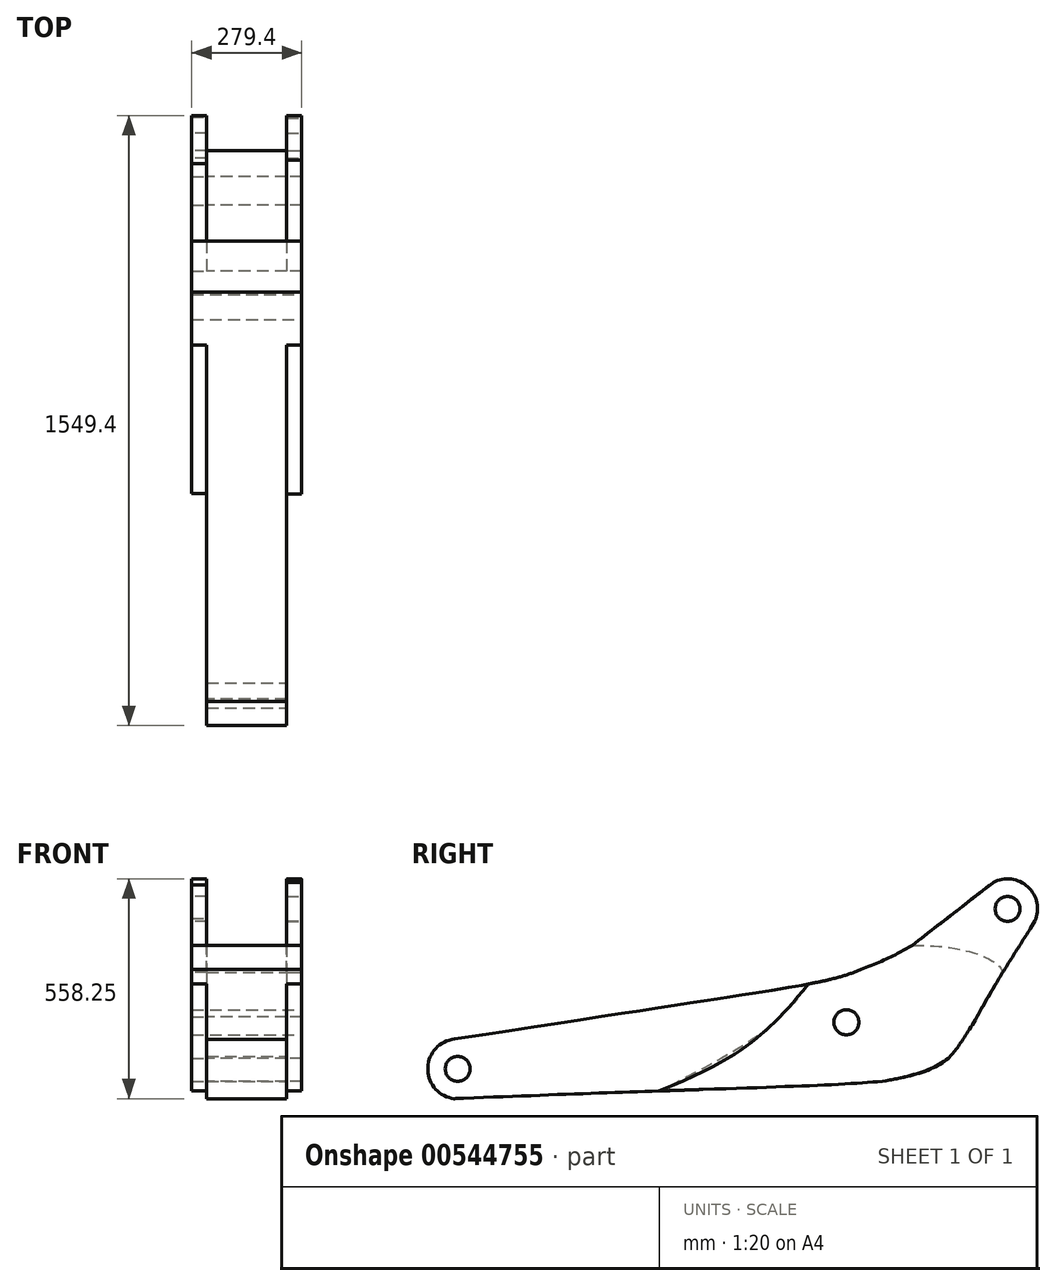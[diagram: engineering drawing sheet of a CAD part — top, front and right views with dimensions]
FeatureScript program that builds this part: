
annotation { "Feature Type Name" : "Feature", "Feature Type Description" : "" }
export const myFeature = defineFeature(function(context is Context, id is Id, definition is map)
    precondition{}
    {
        {
            var Q0;
            Q0=qCreatedBy(makeId("Right.planeOp"),FACE);
            var sketch = newSketch(context, id + "F0", { "sketchPlane" : qUnion([Q0])});
            skCircle(sketch, "E0", {"center": v(-987.29, 252.54) * mm, "radius": 76.2 * mm});
            skCircle(sketch, "E1", {"center": v(409.71, 658.94) * mm, "radius": 76.2 * mm});
            skFitSpline(sketch, "E2", {"points": [v(-996.45, 176.89) * mm, v(259.05, 279.13) * mm, v(396.8, 497.25) * mm], "startDerivative": vector(4754, 195.4) * mm, "endDerivative": vector(700.1, 1215.96) * mm});
            skFitSpline(sketch, "E3", {"points": [v(-1002.41, 327.22) * mm, v(37.1, 504.9) * mm, v(167.2, 566.13) * mm], "startDerivative": vector(3705.38, 571.7) * mm, "endDerivative": vector(553.4, 297.99) * mm});
            skFitSpline(sketch, "E4", {"points": [v(167.2, 566.13) * mm, v(396.8, 497.25) * mm], "startDerivative": vector(309.96, 11.48) * mm, "endDerivative": vector(22.96, -126.28) * mm});
            skFitSpline(sketch, "E5", {"points": [v(-364.35, 200.23) * mm, v(-36.22, 481.03) * mm], "startDerivative": vector(328.11, 280.9) * mm, "endDerivative": vector(328.11, 280.9) * mm});
            skFitSpline(sketch, "E6", {"points": [v(167.2, 566.13) * mm, v(374.05, 726.27) * mm], "startDerivative": vector(206.28, 161.2) * mm, "endDerivative": vector(206.28, 161.2) * mm});
            skFitSpline(sketch, "E7", {"points": [v(396.8, 497.25) * mm, v(480.72, 631.3) * mm], "startDerivative": vector(83.86, 134.07) * mm, "endDerivative": vector(83.86, 134.07) * mm});
            skFitSpline(sketch, "E8", {"points": [v(-36.22, 481.03) * mm, v(37.1, 504.9) * mm, v(117.46, 539.34) * mm, v(167.2, 566.13) * mm], "startDerivative": vector(208.85, 63.05) * mm, "endDerivative": vector(157.2, 89.13) * mm});
            skFitSpline(sketch, "E9", {"points": [v(396.8, 497.25) * mm, v(324.1, 370.97) * mm, v(259.05, 279.13) * mm, v(94.5, 221.73) * mm, v(-364.35, 200.23) * mm], "startDerivative": vector(-361.02, -614.75) * mm, "endDerivative": vector(-1360.38, -16) * mm});
            skPoint(sketch, "E10", {"position": v(0, 370.97) * mm});
            skSolve(sketch);
        }
        {
            var Q0;
            {var subQ5=sQuery(id+"F0.wireOp",EDGE,"E5");Q0=makeQuery(id+"F0.imprint","IMPRINT",FACE,{"disambiguationData":[TD([[makeQuery(id+"F0.imprint","IMPRINT",EDGE,{"derivedFrom":subQ5}),1.0]])]});}
            var Q1;
            {var subQ0=sQuery(id+"F0.wireOp",EDGE,"E4");Q1=makeQuery(id+"F0.imprint","IMPRINT",FACE,{"disambiguationData":[TD([[makeQuery(id+"F0.imprint","IMPRINT",EDGE,{"derivedFrom":subQ0}),-1.0]])]});}
            var Q2;
            {var subQ0=sQuery(id+"F0.wireOp",EDGE,"E2");var subQ1=sQuery(id+"F0.wireOp",EDGE,"E0");var subQ2=makeQuery(id+"F0.imprint","INTERSECT",VERTEX,{"disambiguationData":[OD(0.0)],"derivedFrom":[subQ1,subQ0]});Q2=makeQuery(id+"F0.imprint","IMPRINT",FACE,{"disambiguationData":[TD([[makeQuery(id+"F0.imprint","IMPRINT",EDGE,{"disambiguationData":[TD([[subQ2,1.0]])],"derivedFrom":subQ1}),1.0]])]});}
            extrude(context, id + "F1", {"entities" : qUnion([Q0, Q1, Q2]), "depth" : 203.2 * mm, "offsetDistance" : 25.4 * mm});
        }
        {
            var Q0;
            Q0=makeQuery(id+"F1.opExtrude","CAP_FACE",FACE,{"disambiguationData":[OSD([sQuery(id+"F0.wireOp",EDGE,"E0"),sQuery(id+"F0.wireOp",EDGE,"E1"),sQuery(id+"F0.wireOp",EDGE,"E2"),sQuery(id+"F0.wireOp",EDGE,"E3"),sQuery(id+"F0.wireOp",EDGE,"E6"),sQuery(id+"F0.wireOp",EDGE,"E7"),sQuery(id+"F0.wireOp",EDGE,"E8"),sQuery(id+"F0.wireOp",EDGE,"E9")])],"isStart":false});
            var sketch = newSketch(context, id + "F2", { "sketchPlane" : qUnion([Q0])});
            skPoint(sketch, "E11", {"position": v(-987.29, 252.54) * mm});
            skPoint(sketch, "E12", {"position": v(409.71, 658.94) * mm});
            skPoint(sketch, "E13", {"position": v(0, 370.97) * mm});
            skSolve(sketch);
        }
        {
            var Q0;
            Q0=sQuery(id+"F2.wireOp",VERTEX,"E11");
            var Q1;
            Q1=sQuery(id+"F2.wireOp",VERTEX,"E13");
            var Q2;
            Q2=sQuery(id+"F2.wireOp",VERTEX,"E12");
            var Q3;
            Q3=makeQuery(id+"F1.opExtrude","SWEPT_BODY",BODY,{"disambiguationData":[OSD([sQuery(id+"F0.wireOp",EDGE,"E0"),sQuery(id+"F0.wireOp",EDGE,"E1"),sQuery(id+"F0.wireOp",EDGE,"E2"),sQuery(id+"F0.wireOp",EDGE,"E3"),sQuery(id+"F0.wireOp",EDGE,"E6"),sQuery(id+"F0.wireOp",EDGE,"E7"),sQuery(id+"F0.wireOp",EDGE,"E8"),sQuery(id+"F0.wireOp",EDGE,"E9")])]});
            hole(context, id + "F3", {"style" : HoleStyle.SIMPLE, "endStyle" : HoleEndStyle.THROUGH, "holeDiameter" : 63.5 * mm, "isTappedThrough" : true, "tappedDepth" : 12.7 * mm, "tapClearance" : 3, "locations" : qUnion([Q0, Q1, Q2]), "scope" : qUnion([Q3])});
        }
        {
            var Q0;
            Q0=makeQuery(id+"F1.opExtrude","CAP_FACE",FACE,{"disambiguationData":[OSD([sQuery(id+"F0.wireOp",EDGE,"E0"),sQuery(id+"F0.wireOp",EDGE,"E2"),sQuery(id+"F0.wireOp",EDGE,"E3"),sQuery(id+"F0.wireOp",EDGE,"E4"),sQuery(id+"F0.wireOp",EDGE,"E8"),sQuery(id+"F0.wireOp",EDGE,"E9")])],"isStart":false});
            var sketch = newSketch(context, id + "F4", { "sketchPlane" : qUnion([Q0])});
            skCircle(sketch, "E14", {"center": v(409.71, 658.94) * mm, "radius": 76.2 * mm});
            skPoint(sketch, "E15", {"position": v(-987.29, 252.54) * mm});
            skFitSpline(sketch, "E16", {"points": [v(167.2, 566.13) * mm, v(373.2, 725.82) * mm], "startDerivative": vector(205.34, 160.91) * mm, "endDerivative": vector(205.34, 160.91) * mm});
            skFitSpline(sketch, "E17", {"points": [v(396.8, 497.25) * mm, v(479.44, 628.2) * mm], "startDerivative": vector(82.58, 130.98) * mm, "endDerivative": vector(82.58, 130.98) * mm});
            skFitSpline(sketch, "E18", {"points": [v(-96.78, 468.18) * mm, v(-216.48, 340.33) * mm, v(-475.94, 196.43) * mm], "startDerivative": vector(-328.27, -414.7) * mm, "endDerivative": vector(-773.2, -310.98) * mm});
            skFitSpline(sketch, "E19", {"points": [v(-96.78, 468.18) * mm, v(37.1, 504.9) * mm, v(167.2, 566.13) * mm], "startDerivative": vector(273.15, 62.38) * mm, "endDerivative": vector(254.87, 133.31) * mm});
            skFitSpline(sketch, "E20", {"points": [v(396.8, 497.25) * mm, v(331.4, 384.1) * mm, v(259.05, 279.13) * mm, v(91.08, 221.23) * mm, v(-475.94, 196.43) * mm], "startDerivative": vector(-347.8, -585.35) * mm, "endDerivative": vector(-2799.03, -99.02) * mm});
            skSolve(sketch);
        }
        {
            var Q0;
            {var subQ21=sQuery(id+"F4.wireOp",EDGE,"E18");Q0=makeQuery(id+"F4.imprint","IMPRINT",FACE,{"disambiguationData":[TD([[makeQuery(id+"F4.imprint","IMPRINT",EDGE,{"derivedFrom":subQ21}),1.0]])]});}
            var Q1;
            {var subQ6=sQuery(id+"F0.wireOp",EDGE,"E4");var subQ8=makeQuery(id+"F1.opExtrude","CAP_EDGE",EDGE,{"disambiguationData":[OSD([subQ6])],"isStart":false});Q1=makeQuery(id+"F4.imprint","IMPRINT",FACE,{"disambiguationData":[TD([[makeQuery(id+"F4.imprint","IMPRINT",EDGE,{"derivedFrom":subQ8}),1.0]])]});}
            var Q2;
            {var subQ0=sQuery(id+"F4.wireOp",EDGE,"E16");var subQ1=sQuery(id+"F4.wireOp",EDGE,"E14");var subQ2=makeQuery(id+"F4.imprint","INTERSECT",VERTEX,{"disambiguationData":[OD(1.0)],"derivedFrom":[subQ1,subQ0]});Q2=makeQuery(id+"F4.imprint","IMPRINT",FACE,{"disambiguationData":[TD([[makeQuery(id+"F4.imprint","IMPRINT",EDGE,{"disambiguationData":[TD([[subQ2,-1.0]])],"derivedFrom":subQ1}),1.0]])]});}
            extrude(context, id + "F5", {"entities" : qUnion([Q0, Q1, Q2]), "operationType" : NewBodyOperationType.ADD, "depth" : 25.4 * mm, "offsetDistance" : 25.4 * mm});
        }
        {
            var Q0;
            Q0=makeQuery(id+"F5.opExtrude","CAP_FACE",FACE,{"disambiguationData":[OSD([sQuery(id+"F0.wireOp",EDGE,"E2"),sQuery(id+"F0.wireOp",EDGE,"E3"),sQuery(id+"F0.wireOp",EDGE,"E8"),sQuery(id+"F3.hole-1.sketch.wireOp",EDGE,"core_line_2"),sQuery(id+"F3.hole-1.sketch.wireOp",EDGE,"core_line_3"),sQuery(id+"F4.wireOp",EDGE,"E14"),sQuery(id+"F4.wireOp",EDGE,"E16"),sQuery(id+"F4.wireOp",EDGE,"E17"),sQuery(id+"F4.wireOp",EDGE,"E18"),sQuery(id+"F4.wireOp",EDGE,"E19"),sQuery(id+"F4.wireOp",EDGE,"E20")])],"isStart":false});
            var sketch = newSketch(context, id + "F6", { "sketchPlane" : qUnion([Q0])});
            skPoint(sketch, "E21", {"position": v(409.71, 658.94) * mm});
            skSolve(sketch);
        }
        {
            var Q0;
            Q0=sQuery(id+"F6.wireOp",VERTEX,"E21");
            var Q1;
            Q1=makeQuery(id+"F1.opExtrude","SWEPT_BODY",BODY,{"disambiguationData":[OSD([sQuery(id+"F0.wireOp",EDGE,"E0"),sQuery(id+"F0.wireOp",EDGE,"E2"),sQuery(id+"F0.wireOp",EDGE,"E3"),sQuery(id+"F0.wireOp",EDGE,"E4"),sQuery(id+"F0.wireOp",EDGE,"E8"),sQuery(id+"F0.wireOp",EDGE,"E9")])]});
            hole(context, id + "F7", {"style" : HoleStyle.SIMPLE, "endStyle" : HoleEndStyle.THROUGH, "holeDiameter" : 63.5 * mm, "isTappedThrough" : true, "tappedDepth" : 12.7 * mm, "tapClearance" : 3, "locations" : qUnion([Q0]), "scope" : qUnion([Q1])});
        }
        {
            var Q0;
            Q0=makeQuery(id+"F5.opExtrude","CAP_FACE",FACE,{"disambiguationData":[OSD([sQuery(id+"F0.wireOp",EDGE,"E2"),sQuery(id+"F0.wireOp",EDGE,"E3"),sQuery(id+"F0.wireOp",EDGE,"E8"),sQuery(id+"F3.hole-1.sketch.wireOp",EDGE,"core_line_2"),sQuery(id+"F3.hole-1.sketch.wireOp",EDGE,"core_line_3"),sQuery(id+"F4.wireOp",EDGE,"E14"),sQuery(id+"F4.wireOp",EDGE,"E16"),sQuery(id+"F4.wireOp",EDGE,"E17"),sQuery(id+"F4.wireOp",EDGE,"E18"),sQuery(id+"F4.wireOp",EDGE,"E19"),sQuery(id+"F4.wireOp",EDGE,"E20")])],"isStart":false});
            extrude(context, id + "F8", {"entities" : qUnion([Q0]), "operationType" : NewBodyOperationType.ADD, "depth" : 12.7 * mm, "offsetDistance" : 25.4 * mm});
        }
        {
            var Q0;
            Q0=makeQuery(id+"F1.opExtrude","CAP_FACE",FACE,{"disambiguationData":[OSD([sQuery(id+"F0.wireOp",EDGE,"E0"),sQuery(id+"F0.wireOp",EDGE,"E2"),sQuery(id+"F0.wireOp",EDGE,"E3"),sQuery(id+"F0.wireOp",EDGE,"E4"),sQuery(id+"F0.wireOp",EDGE,"E8"),sQuery(id+"F0.wireOp",EDGE,"E9")])],"isStart":true});
            var sketch = newSketch(context, id + "F9", { "sketchPlane" : qUnion([Q0])});
            skPoint(sketch, "E22", {"position": v(-409.71, 658.94) * mm});
            skCircle(sketch, "E23", {"center": v(-409.71, 658.94) * mm, "radius": 76.2 * mm});
            skFitSpline(sketch, "E24", {"points": [v(-396.8, 497.25) * mm, v(-481.97, 634.73) * mm], "startDerivative": vector(-85.27, 137.45) * mm, "endDerivative": vector(-85.27, 137.45) * mm});
            skFitSpline(sketch, "E25", {"points": [v(-167.2, 566.13) * mm, v(-363.69, 719.67) * mm], "startDerivative": vector(-196.52, 153.48) * mm, "endDerivative": vector(-196.52, 153.48) * mm});
            skFitSpline(sketch, "E26", {"points": [v(-396.8, 497.25) * mm, v(-331.4, 384.1) * mm, v(-259.05, 279.13) * mm, v(-91.08, 221.23) * mm, v(473.96, 196.5) * mm], "startDerivative": vector(347.58, -584.95) * mm, "endDerivative": vector(3014.14, -108.3) * mm});
            skFitSpline(sketch, "E27", {"points": [v(96.7, 468.2) * mm, v(-37.1, 504.9) * mm, v(-167.2, 566.13) * mm], "startDerivative": vector(-291.6, 64.35) * mm, "endDerivative": vector(-256.95, 135.33) * mm});
            skPoint(sketch, "E28", {"position": v(198, 356.95) * mm});
            skFitSpline(sketch, "E29", {"points": [v(96.7, 468.2) * mm, v(198, 356.95) * mm, v(473.96, 196.5) * mm], "startDerivative": vector(204.74, -273.81) * mm, "endDerivative": vector(529.62, -269.82) * mm});
            skSolve(sketch);
        }
        {
            var Q0;
            {var subQ0=sQuery(id+"F9.wireOp",EDGE,"E24");var subQ1=sQuery(id+"F9.wireOp",EDGE,"E23");var subQ2=makeQuery(id+"F9.imprint","INTERSECT",VERTEX,{"disambiguationData":[OD(0.0)],"derivedFrom":[subQ1,subQ0]});Q0=makeQuery(id+"F9.imprint","IMPRINT",FACE,{"disambiguationData":[TD([[makeQuery(id+"F9.imprint","IMPRINT",EDGE,{"disambiguationData":[TD([[subQ2,1.0]])],"derivedFrom":subQ1}),1.0]])]});}
            var Q1;
            {var subQ6=sQuery(id+"F0.wireOp",EDGE,"E4");var subQ8=makeQuery(id+"F1.opExtrude","CAP_EDGE",EDGE,{"disambiguationData":[OSD([subQ6])],"isStart":true});Q1=makeQuery(id+"F9.imprint","IMPRINT",FACE,{"disambiguationData":[TD([[makeQuery(id+"F9.imprint","IMPRINT",EDGE,{"derivedFrom":subQ8}),-1.0]])]});}
            var Q2;
            {var subQ0=sQuery(id+"F9.wireOp",EDGE,"E29");Q2=makeQuery(id+"F9.imprint","IMPRINT",FACE,{"disambiguationData":[TD([[makeQuery(id+"F9.imprint","IMPRINT",EDGE,{"derivedFrom":subQ0}),-1.0]])]});}
            extrude(context, id + "F10", {"entities" : qUnion([Q0, Q1, Q2]), "operationType" : NewBodyOperationType.ADD, "depth" : 38.1 * mm, "offsetDistance" : 25.4 * mm});
        }
        {
            var Q0;
            Q0=makeQuery(id+"F10.opExtrude","CAP_FACE",FACE,{"disambiguationData":[OSD([sQuery(id+"F0.wireOp",EDGE,"E0"),sQuery(id+"F0.wireOp",EDGE,"E2"),sQuery(id+"F0.wireOp",EDGE,"E3"),sQuery(id+"F0.wireOp",EDGE,"E4"),sQuery(id+"F0.wireOp",EDGE,"E8"),sQuery(id+"F0.wireOp",EDGE,"E9"),sQuery(id+"F3.hole-1.sketch.wireOp",EDGE,"core_line_2"),sQuery(id+"F9.wireOp",EDGE,"E23"),sQuery(id+"F9.wireOp",EDGE,"E24"),sQuery(id+"F9.wireOp",EDGE,"E25"),sQuery(id+"F9.wireOp",EDGE,"E26"),sQuery(id+"F9.wireOp",EDGE,"E29")])],"isStart":false});
            var sketch = newSketch(context, id + "F11", { "sketchPlane" : qUnion([Q0])});
            skPoint(sketch, "E30", {"position": v(-409.71, 658.94) * mm});
            skSolve(sketch);
        }
        {
            var Q0;
            Q0=sQuery(id+"F11.wireOp",VERTEX,"E30");
            var Q1;
            Q1=makeQuery(id+"F1.opExtrude","SWEPT_BODY",BODY,{"disambiguationData":[OSD([sQuery(id+"F0.wireOp",EDGE,"E0"),sQuery(id+"F0.wireOp",EDGE,"E2"),sQuery(id+"F0.wireOp",EDGE,"E3"),sQuery(id+"F0.wireOp",EDGE,"E4"),sQuery(id+"F0.wireOp",EDGE,"E8"),sQuery(id+"F0.wireOp",EDGE,"E9")])]});
            hole(context, id + "F12", {"style" : HoleStyle.SIMPLE, "endStyle" : HoleEndStyle.THROUGH, "holeDiameter" : 63.5 * mm, "isTappedThrough" : true, "tappedDepth" : 12.7 * mm, "tapClearance" : 3, "locations" : qUnion([Q0]), "scope" : qUnion([Q1])});
        }
    });
